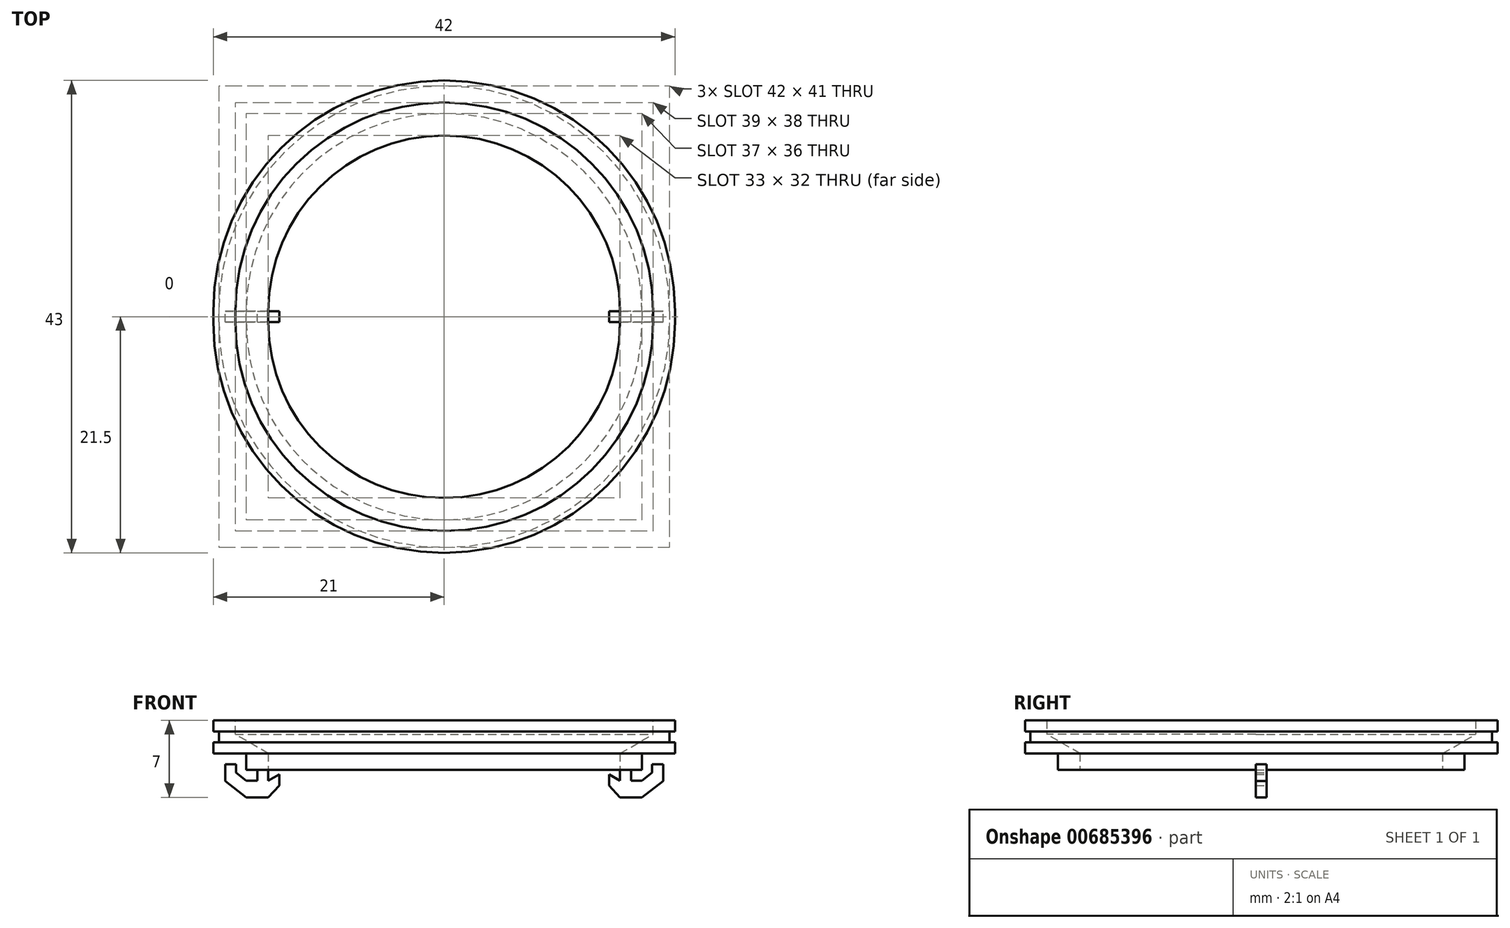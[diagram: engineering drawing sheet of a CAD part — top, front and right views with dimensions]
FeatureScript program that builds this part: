
annotation { "Feature Type Name" : "Feature", "Feature Type Description" : "" }
export const myFeature = defineFeature(function(context is Context, id is Id, definition is map)
    precondition{}
    {
        {
            var Q0;
            Q0=qCreatedBy(makeId("Top.planeOp"),FACE);
            var sketch = newSketch(context, id + "F0", { "sketchPlane" : qUnion([Q0])});
            skLineSegment(sketch, "E0.left", {"start": v(16, 0.5) * mm, "end": v(16, -0.5) * mm});
            skLineSegment(sketch, "E0.right", {"start": v(-16, 0.5) * mm, "end": v(-16, -0.5) * mm});
            skPoint(sketch, "E0.middle", {"position": v(0, 0) * mm});
            skArc(sketch, "E1", {"start": v(16, 0.5) * mm, "mid": v(0, 16.5) * mm, "end": v(-16, 0.5) * mm});
            skArc(sketch, "E2", {"start": v(-16, -0.5) * mm, "mid": v(0, -16.5) * mm, "end": v(16, -0.5) * mm});
            skSolve(sketch);
        }
        {
            var Q0;
            Q0=qCreatedBy(makeId("Front.planeOp"),FACE);
            var sketch = newSketch(context, id + "F1", { "sketchPlane" : qUnion([Q0])});
            skLineSegment(sketch, "E3", {"start": v(18, 0) * mm, "end": v(18, 1.5) * mm});
            skLineSegment(sketch, "E4", {"start": v(18, 1.5) * mm, "end": v(21, 1.5) * mm});
            skLineSegment(sketch, "E5", {"start": v(21, 1.5) * mm, "end": v(21, 2.5) * mm});
            skLineSegment(sketch, "E6", {"start": v(16, 1.5) * mm, "end": v(16, 0) * mm});
            skLineSegment(sketch, "E7", {"start": v(16, 0) * mm, "end": v(18, 0) * mm});
            skLineSegment(sketch, "E8", {"start": v(16, 1.5) * mm, "end": v(19, 3.23) * mm});
            skLineSegment(sketch, "E9", {"start": v(19, 3.23) * mm, "end": v(19, 4.5) * mm});
            skLineSegment(sketch, "E10", {"start": v(19, 4.5) * mm, "end": v(21, 4.5) * mm});
            skLineSegment(sketch, "E11", {"start": v(21, 4.5) * mm, "end": v(21, 3.5) * mm});
            skLineSegment(sketch, "E12", {"start": v(21, 3.5) * mm, "end": v(20.5, 3.5) * mm});
            skLineSegment(sketch, "E13", {"start": v(20.5, 3.5) * mm, "end": v(20.5, 2.5) * mm});
            skLineSegment(sketch, "E14", {"start": v(20.5, 2.5) * mm, "end": v(21, 2.5) * mm});
            skSolve(sketch);
        }
        {
            var Q0;
            Q0=qCreatedBy(makeId("Front.planeOp"),FACE);
            var sketch = newSketch(context, id + "F2", { "sketchPlane" : qUnion([Q0])});
            skLineSegment(sketch, "E15", {"start": v(16, 0) * mm, "end": v(16, -1) * mm});
            skLineSegment(sketch, "E16", {"start": v(16, -2.5) * mm, "end": v(17, -2.5) * mm});
            skLineSegment(sketch, "E17", {"start": v(17, 0) * mm, "end": v(16, 0) * mm});
            skLineSegment(sketch, "E18", {"start": v(16, -1) * mm, "end": v(15, -0.42) * mm});
            skLineSegment(sketch, "E19", {"start": v(15, -0.42) * mm, "end": v(15, -1.42) * mm});
            skLineSegment(sketch, "E20", {"start": v(15, -1.42) * mm, "end": v(16, -2.5) * mm});
            skLineSegment(sketch, "E21", {"start": v(18, -1) * mm, "end": v(17, -1) * mm});
            skLineSegment(sketch, "E22", {"start": v(17, 0) * mm, "end": v(17, -1) * mm});
            skLineSegment(sketch, "E23", {"start": v(19.92, -1.01) * mm, "end": v(19.92, 0.49) * mm});
            skLineSegment(sketch, "E24", {"start": v(19.92, 0.49) * mm, "end": v(18.92, 0.49) * mm});
            skLineSegment(sketch, "E25", {"start": v(18.92, 0.49) * mm, "end": v(18.92, -0.26) * mm});
            skLineSegment(sketch, "E26", {"start": v(18.92, -0.26) * mm, "end": v(18, -1) * mm});
            skLineSegment(sketch, "E27", {"start": v(17, -2.5) * mm, "end": v(18, -2.5) * mm});
            skLineSegment(sketch, "E28", {"start": v(18, -2.5) * mm, "end": v(19.92, -1.01) * mm});
            skLineSegment(sketch, "E29.MirrorCS", {"start": v(-17, 0) * mm, "end": v(-16, 0) * mm});
            skLineSegment(sketch, "E30.MirrorCS", {"start": v(-18.92, -0.26) * mm, "end": v(-18, -1) * mm});
            skLineSegment(sketch, "E31.MirrorCS", {"start": v(-15, -1.42) * mm, "end": v(-16, -2.5) * mm});
            skLineSegment(sketch, "E32.MirrorCS", {"start": v(-16, -1) * mm, "end": v(-15, -0.42) * mm});
            skLineSegment(sketch, "E33.MirrorCS", {"start": v(-18, -1) * mm, "end": v(-17, -1) * mm});
            skLineSegment(sketch, "E34.MirrorCS", {"start": v(-18, -2.5) * mm, "end": v(-19.92, -1.01) * mm});
            skLineSegment(sketch, "E35.MirrorCS", {"start": v(-15, -0.42) * mm, "end": v(-15, -1.42) * mm});
            skLineSegment(sketch, "E36.MirrorCS", {"start": v(-19.92, -1.01) * mm, "end": v(-19.92, 0.49) * mm});
            skLineSegment(sketch, "E37.MirrorCS", {"start": v(-17, -2.5) * mm, "end": v(-18, -2.5) * mm});
            skLineSegment(sketch, "E38.MirrorCS", {"start": v(-18.92, 0.49) * mm, "end": v(-18.92, -0.26) * mm});
            skLineSegment(sketch, "E39.MirrorCS", {"start": v(-17, 0) * mm, "end": v(-17, -1) * mm});
            skLineSegment(sketch, "E40.MirrorCS", {"start": v(-16, 0) * mm, "end": v(-16, -1) * mm});
            skLineSegment(sketch, "E41.MirrorCS", {"start": v(-19.92, 0.49) * mm, "end": v(-18.92, 0.49) * mm});
            skLineSegment(sketch, "E42.MirrorCS", {"start": v(-16, -2.5) * mm, "end": v(-17, -2.5) * mm});
            skSolve(sketch);
        }
        {
            var Q0;
            Q0=makeQuery(id+"F2.imprint","IMPRINT",FACE,{"disambiguationData":[TD([[makeQuery(id+"F2.imprint","IMPRINT",EDGE,{"derivedFrom":sQuery(id+"F2.wireOp",EDGE,"E29.MirrorCS")}),-1.0]])]});
            var Q1;
            Q1=makeQuery(id+"F2.imprint","IMPRINT",FACE,{"disambiguationData":[TD([[makeQuery(id+"F2.imprint","IMPRINT",EDGE,{"derivedFrom":sQuery(id+"F2.wireOp",EDGE,"E15")}),1.0]])]});
            extrude(context, id + "F3", {"entities" : qUnion([Q0, Q1]), "depth" : 1 * mm, "offsetDistance" : 25 * mm, "symmetric" : true});
        }
        {
            var Q0;
            Q0=makeQuery(id+"F1.imprint","IMPRINT",FACE,{"disambiguationData":[TD([[makeQuery(id+"F1.imprint","IMPRINT",EDGE,{"derivedFrom":sQuery(id+"F1.wireOp",EDGE,"E3")}),1.0]])]});
            var Q1;
            Q1=sQuery(id+"F0.wireOp",EDGE,"E2");
            var Q2;
            Q2=sQuery(id+"F0.wireOp",EDGE,"E0.right");
            var Q3;
            Q3=sQuery(id+"F0.wireOp",EDGE,"E1");
            var Q4;
            Q4=sQuery(id+"F0.wireOp",EDGE,"E0.left");
            sweep(context, id + "F4", {"profiles" : qUnion([Q0]), "path" : qUnion([Q1, Q2, Q3, Q4])});
        }
    });
